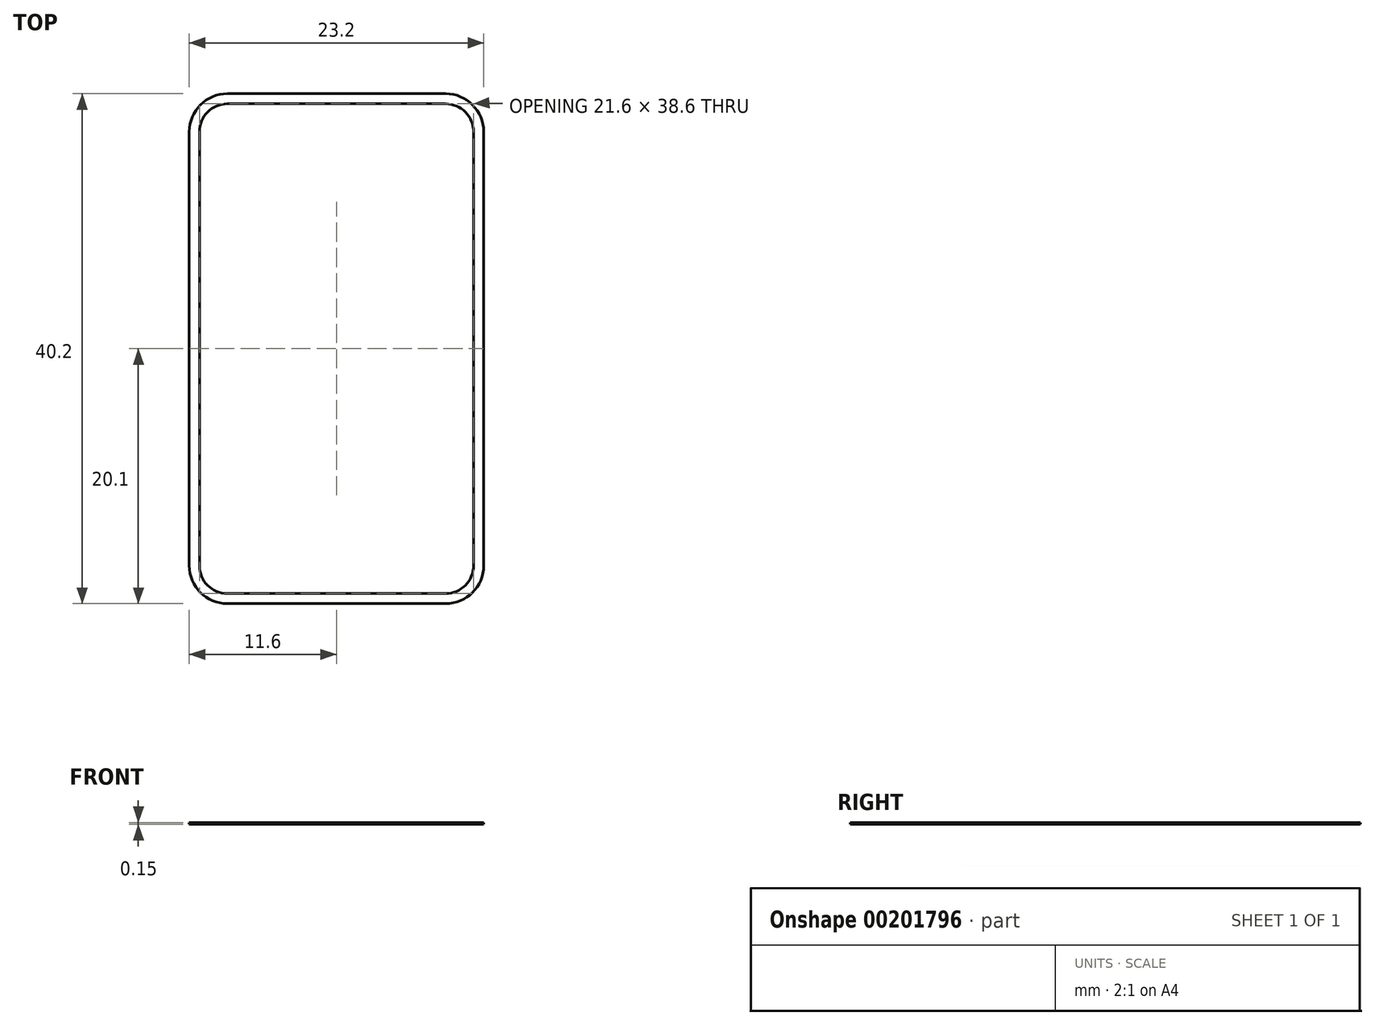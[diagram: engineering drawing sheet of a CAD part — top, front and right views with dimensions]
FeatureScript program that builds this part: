
annotation { "Feature Type Name" : "Feature", "Feature Type Description" : "" }
export const myFeature = defineFeature(function(context is Context, id is Id, definition is map)
    precondition{}
    {
        {
            var Q0;
            Q0=qCreatedBy(makeId("Top.planeOp"),FACE);
            var sketch = newSketch(context, id + "F0", { "sketchPlane" : qUnion([Q0])});
            skLineSegment(sketch, "E0.bottom", {"start": v(-11.2, 19.7) * mm, "end": v(11.2, 19.7) * mm, "construction": true});
            skLineSegment(sketch, "E0.top", {"start": v(-11.2, -19.7) * mm, "end": v(11.2, -19.7) * mm, "construction": true});
            skLineSegment(sketch, "E0.left", {"start": v(-11.2, 19.7) * mm, "end": v(-11.2, -19.7) * mm, "construction": true});
            skLineSegment(sketch, "E0.right", {"start": v(11.2, 19.7) * mm, "end": v(11.2, -19.7) * mm, "construction": true});
            skPoint(sketch, "E1", {"position": v(0, 19.7) * mm});
            skPoint(sketch, "E2", {"position": v(11.2, 0) * mm});
            skLineSegment(sketch, "E3.bottom", {"start": v(-10.8, 19.3) * mm, "end": v(10.8, 19.3) * mm});
            skLineSegment(sketch, "E3.top", {"start": v(-10.8, -19.3) * mm, "end": v(10.8, -19.3) * mm});
            skLineSegment(sketch, "E3.left", {"start": v(-10.8, 19.3) * mm, "end": v(-10.8, -19.3) * mm});
            skLineSegment(sketch, "E3.right", {"start": v(10.8, 19.3) * mm, "end": v(10.8, -19.3) * mm});
            skLineSegment(sketch, "E4.bottom", {"start": v(-11.6, 20.1) * mm, "end": v(11.6, 20.1) * mm});
            skLineSegment(sketch, "E4.top", {"start": v(-11.6, -20.1) * mm, "end": v(11.6, -20.1) * mm});
            skLineSegment(sketch, "E4.left", {"start": v(-11.6, 20.1) * mm, "end": v(-11.6, -20.1) * mm});
            skLineSegment(sketch, "E4.right", {"start": v(11.6, 20.1) * mm, "end": v(11.6, -20.1) * mm});
            skPoint(sketch, "E5", {"position": v(0, 20.1) * mm});
            skPoint(sketch, "E6", {"position": v(11.6, 0) * mm});
            skPoint(sketch, "E7", {"position": v(0, 19.3) * mm});
            skPoint(sketch, "E8", {"position": v(10.8, 0) * mm});
            skLineSegment(sketch, "E9", {"start": v(-11.6, 0) * mm, "end": v(-10.8, 0) * mm, "construction": true});
            skLineSegment(sketch, "E10", {"start": v(0, 20.1) * mm, "end": v(0, 19.3) * mm, "construction": true});
            skPoint(sketch, "E11", {"position": v(-11.2, 0) * mm});
            skSolve(sketch);
        }
        {
            var Q0;
            Q0 = qSketchRegion(id + "F0", true);
            extrude(context, id + "F1", {"entities" : qUnion([Q0]), "oppositeDirection" : true, "depth" : .15 * mm});
        }
        {
            var Q0;
            Q0=makeQuery(id+"F1.opExtrude","SWEPT_EDGE",EDGE,{"disambiguationData":[OSD([sQuery(id+"F0.wireOp",EDGE,"E3.top"),sQuery(id+"F0.wireOp",EDGE,"E3.right")])]});
            var Q1;
            Q1=makeQuery(id+"F1.opExtrude","SWEPT_EDGE",EDGE,{"disambiguationData":[OSD([sQuery(id+"F0.wireOp",EDGE,"E3.top"),sQuery(id+"F0.wireOp",EDGE,"E3.left")])]});
            var Q2;
            Q2=makeQuery(id+"F1.opExtrude","SWEPT_EDGE",EDGE,{"disambiguationData":[OSD([sQuery(id+"F0.wireOp",EDGE,"E3.bottom"),sQuery(id+"F0.wireOp",EDGE,"E3.right")])]});
            var Q3;
            Q3=makeQuery(id+"F1.opExtrude","SWEPT_EDGE",EDGE,{"disambiguationData":[OSD([sQuery(id+"F0.wireOp",EDGE,"E3.bottom"),sQuery(id+"F0.wireOp",EDGE,"E3.left")])]});
            fillet(context, id + "F2", {"entities" : qUnion([Q0, Q1, Q2, Q3]), "radius" : 2.2 * mm, "tangentPropagation" : true, "allowEdgeOverflow" : false});
        }
        {
            var Q0;
            Q0=makeQuery(id+"F1.opExtrude","SWEPT_EDGE",EDGE,{"disambiguationData":[OSD([sQuery(id+"F0.wireOp",EDGE,"E4.top"),sQuery(id+"F0.wireOp",EDGE,"E4.left")])]});
            var Q1;
            Q1=makeQuery(id+"F1.opExtrude","SWEPT_EDGE",EDGE,{"disambiguationData":[OSD([sQuery(id+"F0.wireOp",EDGE,"E4.top"),sQuery(id+"F0.wireOp",EDGE,"E4.right")])]});
            var Q2;
            Q2=makeQuery(id+"F1.opExtrude","SWEPT_EDGE",EDGE,{"disambiguationData":[OSD([sQuery(id+"F0.wireOp",EDGE,"E4.bottom"),sQuery(id+"F0.wireOp",EDGE,"E4.right")])]});
            var Q3;
            Q3=makeQuery(id+"F1.opExtrude","SWEPT_EDGE",EDGE,{"disambiguationData":[OSD([sQuery(id+"F0.wireOp",EDGE,"E4.bottom"),sQuery(id+"F0.wireOp",EDGE,"E4.left")])]});
            fillet(context, id + "F3", {"entities" : qUnion([Q0, Q1, Q2, Q3]), "radius" : 3 * mm, "tangentPropagation" : true, "allowEdgeOverflow" : false});
        }
    });
